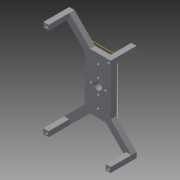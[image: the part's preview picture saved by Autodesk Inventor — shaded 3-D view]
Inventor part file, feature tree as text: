
AUTODESK INVENTOR PART (.ipt)
format: ipt  version: 2015 (Build 190159000, 159)  size: 187,904 bytes
history: native  units: in
note: dims shown in document units (in); Inventor stores cm internally (conversion verified against a paired STEP export)
features: extrude x3, sketch x3, plane x1, reference x1
ambient origin geometry x8: Origin, YZ Plane, XZ Plane, XY Plane, X Axis, Y Axis, Z Axis, Center Point
bodies: Solid1 (feature_tree)
feature tree (8):
  plane  "Work Plane1"
  extrude  "Extrusion1"  Depth=0.7874in
  extrude  "Extrusion3"  Depth=0.7874in
  extrude  "Extrusion4"  Depth=0.7874in
  sketch  "Sketch1"  dims[d0=0.1969in d1=0.0in d16=0.7874in]
  reference  "Reference1"
  sketch  "Sketch4"  dims[d17=0.7874in d18=0.7874in]
  sketch  "Sketch5"  dims[d19=0.7874in d20=0.7874in d21=0.7874in d22=0.7874in d23=0.7874in d24=0.1969in d25=0.1969in d26=0.1969in d27=0.1969in d28=0.1969in d29=0.1969in d30=0.1969in d31=0.1969in d32=0.1969in d33=0.1969in d34=0.1969in d35=0.1969in d36=0.1969in d37=0.1969in d38=0.1969in d39=0.1969in d40=0.1181in d41=0.1969in d42=0.0in d43=0.7874in d44=0.0in]
